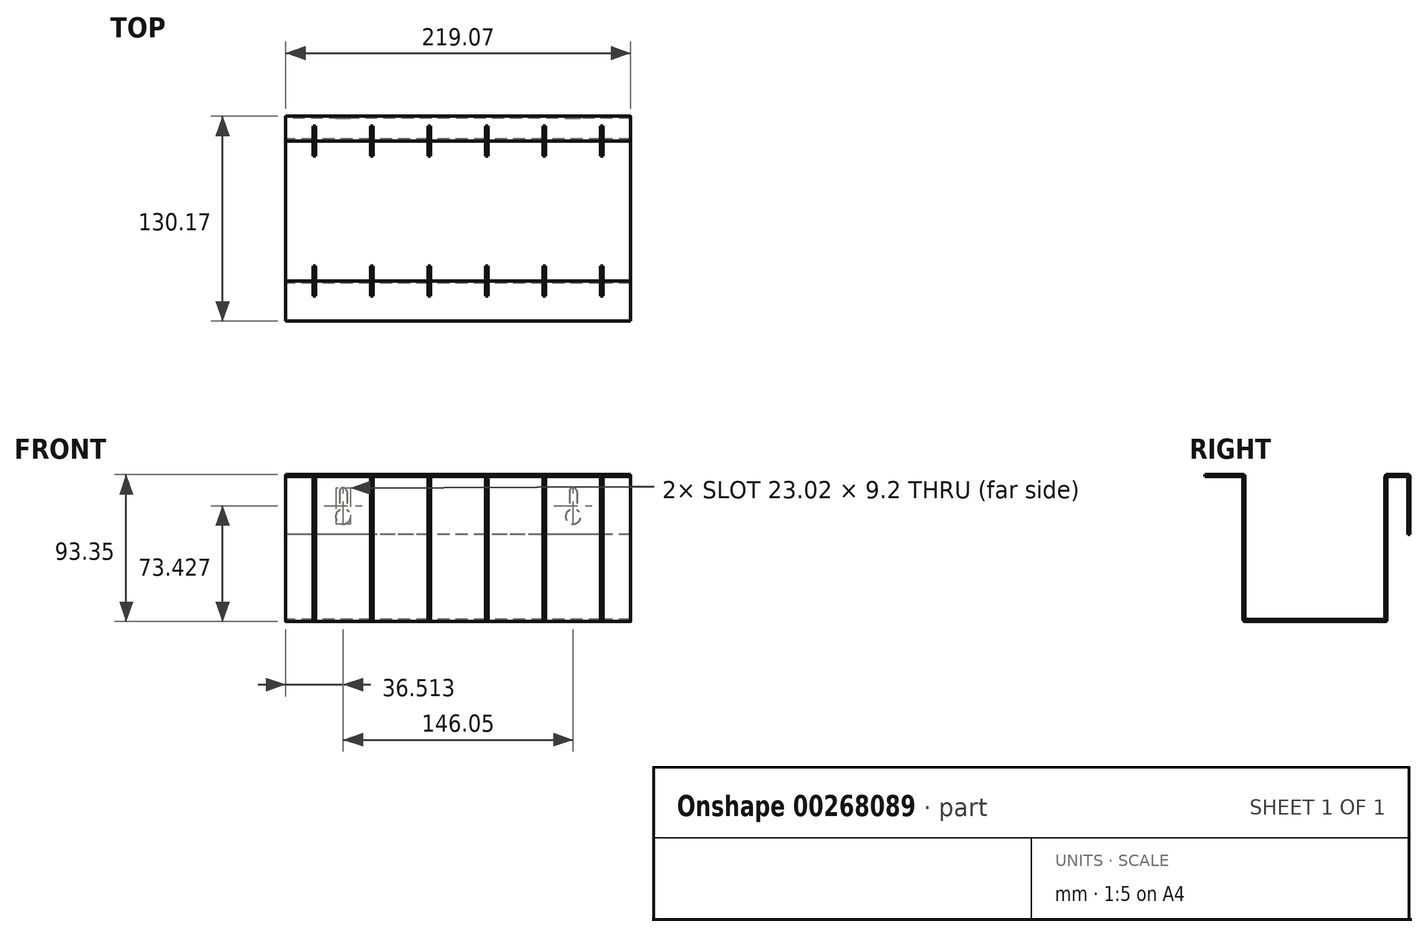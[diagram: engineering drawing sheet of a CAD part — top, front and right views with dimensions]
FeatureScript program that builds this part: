
annotation { "Feature Type Name" : "Feature", "Feature Type Description" : "" }
export const myFeature = defineFeature(function(context is Context, id is Id, definition is map)
    precondition{}
    {
        {
            var Q0;
            Q0=qCreatedBy(makeId("Right.planeOp"),FACE);
            var sketch = newSketch(context, id + "F0", { "sketchPlane" : qUnion([Q0])});
            skLineSegment(sketch, "E0", {"start": v(-62.66, 38.1) * mm, "end": v(-37.26, 38.1) * mm});
            skLineSegment(sketch, "E1", {"start": v(-37.26, 38.1) * mm, "end": v(-37.26, -53.98) * mm});
            skLineSegment(sketch, "E2", {"start": v(-37.26, -53.98) * mm, "end": v(51.64, -53.98) * mm});
            skLineSegment(sketch, "E3", {"start": v(51.64, -53.98) * mm, "end": v(51.64, 38.1) * mm});
            skLineSegment(sketch, "E4", {"start": v(51.64, 38.1) * mm, "end": v(67.51, 38.1) * mm});
            skLineSegment(sketch, "E5", {"start": v(67.51, 38.1) * mm, "end": v(67.51, 0) * mm});
            skLineSegment(sketch, "E6.0", {"start": v(66.24, 36.83) * mm, "end": v(66.24, 0) * mm});
            skLineSegment(sketch, "E6.1", {"start": v(52.9, 36.83) * mm, "end": v(66.24, 36.83) * mm});
            skLineSegment(sketch, "E6.2", {"start": v(-62.66, 36.83) * mm, "end": v(-38.53, 36.83) * mm});
            skLineSegment(sketch, "E6.3", {"start": v(-38.53, 36.83) * mm, "end": v(-38.53, -55.25) * mm});
            skLineSegment(sketch, "E6.4", {"start": v(-38.53, -55.25) * mm, "end": v(52.9, -55.25) * mm});
            skLineSegment(sketch, "E6.5", {"start": v(52.9, -55.25) * mm, "end": v(52.9, 36.83) * mm});
            skLineSegment(sketch, "E7", {"start": v(66.24, 0) * mm, "end": v(67.51, 0) * mm});
            skLineSegment(sketch, "E8", {"start": v(-62.66, 38.1) * mm, "end": v(-62.66, 36.83) * mm});
            skSolve(sketch);
        }
        {
            var Q0;
            Q0 = qSketchRegion(id + "F0", true);
            extrude(context, id + "F1", {"entities" : qUnion([Q0]), "depth" : 219.07 * mm});
        }
        {
            var Q0;
            Q0=makeQuery(id+"F1.opExtrude","SWEPT_FACE",FACE,{"disambiguationData":[OSD([sQuery(id+"F0.wireOp",EDGE,"E0")])]});
            var sketch = newSketch(context, id + "F2", { "sketchPlane" : qUnion([Q0])});
            skLineSegment(sketch, "E9", {"start": v(219.08, -46.79) * mm, "end": v(0, -46.79) * mm, "construction": true});
            skLineSegment(sketch, "E10", {"start": v(17.46, -46.79) * mm, "end": v(17.46, -27.73) * mm});
            skLineSegment(sketch, "E11", {"start": v(19.05, -46.79) * mm, "end": v(19.05, -27.73) * mm});
            skLineSegment(sketch, "E12", {"start": v(19.05, -27.73) * mm, "end": v(17.46, -27.73) * mm});
            skLineSegment(sketch, "E13", {"start": v(17.46, -46.79) * mm, "end": v(19.05, -46.79) * mm});
            skLineSegment(sketch, "E14", {"start": v(201.61, -62.66) * mm, "end": v(201.61, -37.26) * mm, "construction": true});
            skSolve(sketch);
        }
        {
            var Q0;
            Q0 = qSketchRegion(id + "F2", true);
            extrude(context, id + "F3", {"entities" : qUnion([Q0]), "operationType" : NewBodyOperationType.REMOVE, "oppositeDirection" : true, "depth" : 97.28 * mm});
        }
        {
            var Q0;
            Q0=makeQuery(id+"F1.opExtrude","SWEPT_FACE",FACE,{"disambiguationData":[OSD([sQuery(id+"F0.wireOp",EDGE,"E0")])]});
            var sketch = newSketch(context, id + "F4", { "sketchPlane" : qUnion([Q0])});
            skLineSegment(sketch, "E15", {"start": v(53.98, -46.79) * mm, "end": v(53.98, -27.74) * mm});
            skLineSegment(sketch, "E16", {"start": v(55.56, -46.79) * mm, "end": v(55.56, -27.74) * mm});
            skLineSegment(sketch, "E17", {"start": v(55.56, -46.79) * mm, "end": v(53.98, -46.79) * mm});
            skLineSegment(sketch, "E18", {"start": v(55.56, -27.74) * mm, "end": v(53.98, -27.74) * mm});
            skLineSegment(sketch, "E19", {"start": v(90.49, -46.79) * mm, "end": v(90.49, -27.74) * mm});
            skLineSegment(sketch, "E20", {"start": v(92.08, -46.79) * mm, "end": v(92.08, -27.74) * mm});
            skLineSegment(sketch, "E21", {"start": v(92.08, -46.79) * mm, "end": v(90.49, -46.79) * mm});
            skLineSegment(sketch, "E22", {"start": v(92.08, -27.74) * mm, "end": v(90.49, -27.74) * mm});
            skLineSegment(sketch, "E23", {"start": v(127, -46.79) * mm, "end": v(127, -27.74) * mm});
            skLineSegment(sketch, "E24", {"start": v(128.59, -46.79) * mm, "end": v(128.59, -27.74) * mm});
            skLineSegment(sketch, "E25", {"start": v(128.59, -46.79) * mm, "end": v(127, -46.79) * mm});
            skLineSegment(sketch, "E26", {"start": v(128.59, -27.74) * mm, "end": v(127, -27.74) * mm});
            skLineSegment(sketch, "E27", {"start": v(163.51, -46.79) * mm, "end": v(163.51, -27.74) * mm});
            skLineSegment(sketch, "E28", {"start": v(165.1, -46.79) * mm, "end": v(165.1, -27.74) * mm});
            skLineSegment(sketch, "E29", {"start": v(165.1, -46.79) * mm, "end": v(163.51, -46.79) * mm});
            skLineSegment(sketch, "E30", {"start": v(165.1, -27.74) * mm, "end": v(163.51, -27.74) * mm});
            skLineSegment(sketch, "E31", {"start": v(200.03, -46.79) * mm, "end": v(200.03, -27.74) * mm});
            skLineSegment(sketch, "E32", {"start": v(201.61, -46.79) * mm, "end": v(201.61, -27.74) * mm});
            skLineSegment(sketch, "E33", {"start": v(201.61, -46.79) * mm, "end": v(200.03, -46.79) * mm});
            skLineSegment(sketch, "E34", {"start": v(201.61, -27.74) * mm, "end": v(200.03, -27.74) * mm});
            skSolve(sketch);
        }
        {
            var Q0;
            Q0 = qSketchRegion(id + "F4", true);
            extrude(context, id + "F5", {"entities" : qUnion([Q0]), "operationType" : NewBodyOperationType.REMOVE, "endBound" : BoundingType.THROUGH_ALL, "oppositeDirection" : true, "depth" : 108.97 * mm});
        }
        {
            var Q0;
            Q0=makeQuery(id+"F1.opExtrude","SWEPT_FACE",FACE,{"disambiguationData":[OSD([sQuery(id+"F0.wireOp",EDGE,"E0")])]});
            var sketch = newSketch(context, id + "F6", { "sketchPlane" : qUnion([Q0])});
            skSolve(sketch);
        }
        {
            var Q0;
            {var subQ0=sQuery(id+"F0.wireOp",EDGE,"E4");Q0=makeQuery(id+"F7m0HWUFy6dzAhm_1.boolean.opBoolean","MERGE",FACE,{"derivedFrom":[makeQuery(id+"F1.opExtrude","SWEPT_FACE",FACE,{"disambiguationData":[OSD([subQ0])]}),makeQuery(id+"F7m0HWUFy6dzAhm_1.opExtrude","SWEPT_FACE",FACE,{"disambiguationData":[OSD([subQ0])]})]});}
            var sketch = newSketch(context, id + "F7", { "sketchPlane" : qUnion([Q0])});
            skLineSegment(sketch, "E35", {"start": v(17.46, 61.16) * mm, "end": v(17.46, 42.11) * mm});
            skLineSegment(sketch, "E36", {"start": v(19.05, 61.16) * mm, "end": v(19.05, 42.11) * mm});
            skLineSegment(sketch, "E37", {"start": v(17.46, 61.16) * mm, "end": v(19.05, 61.16) * mm});
            skLineSegment(sketch, "E38", {"start": v(17.46, 42.11) * mm, "end": v(19.05, 42.11) * mm});
            skLineSegment(sketch, "E39", {"start": v(53.98, 61.16) * mm, "end": v(53.98, 42.11) * mm});
            skLineSegment(sketch, "E40", {"start": v(55.56, 61.16) * mm, "end": v(55.56, 42.11) * mm});
            skLineSegment(sketch, "E41", {"start": v(55.56, 42.11) * mm, "end": v(53.98, 42.11) * mm});
            skLineSegment(sketch, "E42", {"start": v(55.56, 61.16) * mm, "end": v(53.98, 61.16) * mm});
            skLineSegment(sketch, "E43", {"start": v(90.49, 61.16) * mm, "end": v(90.49, 42.11) * mm});
            skLineSegment(sketch, "E44", {"start": v(90.49, 42.11) * mm, "end": v(92.08, 42.11) * mm});
            skLineSegment(sketch, "E45", {"start": v(92.08, 42.11) * mm, "end": v(92.08, 61.16) * mm});
            skLineSegment(sketch, "E46", {"start": v(90.49, 61.16) * mm, "end": v(92.08, 61.16) * mm});
            skLineSegment(sketch, "E47", {"start": v(127, 61.16) * mm, "end": v(127, 42.11) * mm});
            skLineSegment(sketch, "E48", {"start": v(127, 42.11) * mm, "end": v(128.59, 42.11) * mm});
            skLineSegment(sketch, "E49", {"start": v(128.59, 42.11) * mm, "end": v(128.59, 61.16) * mm});
            skLineSegment(sketch, "E50", {"start": v(127, 61.16) * mm, "end": v(128.59, 61.16) * mm});
            skLineSegment(sketch, "E51", {"start": v(163.51, 61.16) * mm, "end": v(163.51, 42.11) * mm});
            skLineSegment(sketch, "E52", {"start": v(163.51, 42.11) * mm, "end": v(165.1, 42.11) * mm});
            skLineSegment(sketch, "E53", {"start": v(165.1, 42.11) * mm, "end": v(165.1, 61.16) * mm});
            skLineSegment(sketch, "E54", {"start": v(165.1, 61.16) * mm, "end": v(163.51, 61.16) * mm});
            skLineSegment(sketch, "E55", {"start": v(200.03, 61.16) * mm, "end": v(200.03, 42.11) * mm});
            skLineSegment(sketch, "E56", {"start": v(200.03, 42.11) * mm, "end": v(201.61, 42.11) * mm});
            skLineSegment(sketch, "E57", {"start": v(201.61, 42.11) * mm, "end": v(201.61, 61.16) * mm});
            skLineSegment(sketch, "E58", {"start": v(200.03, 61.16) * mm, "end": v(201.61, 61.16) * mm});
            skSolve(sketch);
        }
        {
            var Q0;
            Q0 = qSketchRegion(id + "F7", true);
            extrude(context, id + "F8", {"entities" : qUnion([Q0]), "operationType" : NewBodyOperationType.REMOVE, "oppositeDirection" : true, "depth" : 134.62 * mm});
        }
        {
            var Q0;
            {var subQ0=sQuery(id+"F0.wireOp",EDGE,"E6.1");var subQ1=sQuery(id+"F0.wireOp",EDGE,"E6.0");Q0=makeQuery(id+"F7m0HWUFy6dzAhm_1.boolean.opBoolean","MERGE",EDGE,{"derivedFrom":[makeQuery(id+"F1.opExtrude","SWEPT_EDGE",EDGE,{"disambiguationData":[OSD([subQ1,subQ0])]}),makeQuery(id+"F7m0HWUFy6dzAhm_1.opExtrude","SWEPT_EDGE",EDGE,{"disambiguationData":[OSD([subQ1,subQ0])]})]});}
            var Q1;
            {var subQ0=sQuery(id+"F0.wireOp",EDGE,"E6.5");var subQ1=sQuery(id+"F0.wireOp",EDGE,"E6.1");Q1=makeQuery(id+"F8.boolean.opBoolean","SPLIT",EDGE,{"disambiguationData":[TD([makeQuery(id+"F8.opExtrude","SWEPT_FACE",FACE,{"disambiguationData":[OSD([sQuery(id+"F7.wireOp",EDGE,"E57")])]})])],"derivedFrom":makeQuery(id+"F7m0HWUFy6dzAhm_1.boolean.opBoolean","MERGE",EDGE,{"derivedFrom":[makeQuery(id+"F1.opExtrude","SWEPT_EDGE",EDGE,{"disambiguationData":[OSD([subQ1,subQ0])]}),makeQuery(id+"F7m0HWUFy6dzAhm_1.opExtrude","SWEPT_EDGE",EDGE,{"disambiguationData":[OSD([subQ1,subQ0])]})]})});}
            var Q2;
            {var subQ0=sQuery(id+"F0.wireOp",EDGE,"E6.5");var subQ1=sQuery(id+"F0.wireOp",EDGE,"E6.1");Q2=makeQuery(id+"F8.boolean.opBoolean","SPLIT",EDGE,{"disambiguationData":[TD([makeQuery(id+"F8.opExtrude","SWEPT_FACE",FACE,{"disambiguationData":[OSD([sQuery(id+"F7.wireOp",EDGE,"E53")])]})])],"derivedFrom":makeQuery(id+"F7m0HWUFy6dzAhm_1.boolean.opBoolean","MERGE",EDGE,{"derivedFrom":[makeQuery(id+"F1.opExtrude","SWEPT_EDGE",EDGE,{"disambiguationData":[OSD([subQ1,subQ0])]}),makeQuery(id+"F7m0HWUFy6dzAhm_1.opExtrude","SWEPT_EDGE",EDGE,{"disambiguationData":[OSD([subQ1,subQ0])]})]})});}
            var Q3;
            {var subQ0=sQuery(id+"F0.wireOp",EDGE,"E6.5");var subQ1=sQuery(id+"F0.wireOp",EDGE,"E6.1");Q3=makeQuery(id+"F8.boolean.opBoolean","SPLIT",EDGE,{"disambiguationData":[TD([makeQuery(id+"F8.opExtrude","SWEPT_FACE",FACE,{"disambiguationData":[OSD([sQuery(id+"F7.wireOp",EDGE,"E49")])]})])],"derivedFrom":makeQuery(id+"F7m0HWUFy6dzAhm_1.boolean.opBoolean","MERGE",EDGE,{"derivedFrom":[makeQuery(id+"F1.opExtrude","SWEPT_EDGE",EDGE,{"disambiguationData":[OSD([subQ1,subQ0])]}),makeQuery(id+"F7m0HWUFy6dzAhm_1.opExtrude","SWEPT_EDGE",EDGE,{"disambiguationData":[OSD([subQ1,subQ0])]})]})});}
            var Q4;
            {var subQ0=sQuery(id+"F0.wireOp",EDGE,"E6.5");var subQ1=sQuery(id+"F0.wireOp",EDGE,"E6.1");Q4=makeQuery(id+"F8.boolean.opBoolean","SPLIT",EDGE,{"disambiguationData":[TD([makeQuery(id+"F8.opExtrude","SWEPT_FACE",FACE,{"disambiguationData":[OSD([sQuery(id+"F7.wireOp",EDGE,"E45")])]})])],"derivedFrom":makeQuery(id+"F7m0HWUFy6dzAhm_1.boolean.opBoolean","MERGE",EDGE,{"derivedFrom":[makeQuery(id+"F1.opExtrude","SWEPT_EDGE",EDGE,{"disambiguationData":[OSD([subQ1,subQ0])]}),makeQuery(id+"F7m0HWUFy6dzAhm_1.opExtrude","SWEPT_EDGE",EDGE,{"disambiguationData":[OSD([subQ1,subQ0])]})]})});}
            var Q5;
            {var subQ0=sQuery(id+"F0.wireOp",EDGE,"E6.5");var subQ1=sQuery(id+"F0.wireOp",EDGE,"E6.1");Q5=makeQuery(id+"F8.boolean.opBoolean","SPLIT",EDGE,{"disambiguationData":[TD([makeQuery(id+"F8.opExtrude","SWEPT_FACE",FACE,{"disambiguationData":[OSD([sQuery(id+"F7.wireOp",EDGE,"E40")])]})])],"derivedFrom":makeQuery(id+"F7m0HWUFy6dzAhm_1.boolean.opBoolean","MERGE",EDGE,{"derivedFrom":[makeQuery(id+"F1.opExtrude","SWEPT_EDGE",EDGE,{"disambiguationData":[OSD([subQ1,subQ0])]}),makeQuery(id+"F7m0HWUFy6dzAhm_1.opExtrude","SWEPT_EDGE",EDGE,{"disambiguationData":[OSD([subQ1,subQ0])]})]})});}
            var Q6;
            {var subQ0=sQuery(id+"F0.wireOp",EDGE,"E6.5");var subQ1=sQuery(id+"F0.wireOp",EDGE,"E6.1");Q6=makeQuery(id+"F8.boolean.opBoolean","SPLIT",EDGE,{"disambiguationData":[TD([makeQuery(id+"F8.opExtrude","SWEPT_FACE",FACE,{"disambiguationData":[OSD([sQuery(id+"F7.wireOp",EDGE,"E36")])]})])],"derivedFrom":makeQuery(id+"F7m0HWUFy6dzAhm_1.boolean.opBoolean","MERGE",EDGE,{"derivedFrom":[makeQuery(id+"F1.opExtrude","SWEPT_EDGE",EDGE,{"disambiguationData":[OSD([subQ1,subQ0])]}),makeQuery(id+"F7m0HWUFy6dzAhm_1.opExtrude","SWEPT_EDGE",EDGE,{"disambiguationData":[OSD([subQ1,subQ0])]})]})});}
            var Q7;
            {var subQ0=sQuery(id+"F0.wireOp",EDGE,"E6.5");var subQ1=sQuery(id+"F0.wireOp",EDGE,"E6.1");Q7=makeQuery(id+"F8.boolean.opBoolean","SPLIT",EDGE,{"disambiguationData":[TD([makeQuery(id+"F8.opExtrude","SWEPT_FACE",FACE,{"disambiguationData":[OSD([sQuery(id+"F7.wireOp",EDGE,"E35")])]})])],"derivedFrom":makeQuery(id+"F7m0HWUFy6dzAhm_1.boolean.opBoolean","MERGE",EDGE,{"derivedFrom":[makeQuery(id+"F1.opExtrude","SWEPT_EDGE",EDGE,{"disambiguationData":[OSD([subQ1,subQ0])]}),makeQuery(id+"F7m0HWUFy6dzAhm_1.opExtrude","SWEPT_EDGE",EDGE,{"disambiguationData":[OSD([subQ1,subQ0])]})]})});}
            var Q8;
            {var subQ0=sQuery(id+"F0.wireOp",EDGE,"E6.3");var subQ1=sQuery(id+"F0.wireOp",EDGE,"E6.2");Q8=makeQuery(id+"F7m0HWUFy6dzAhm_1.boolean.opBoolean","MERGE",EDGE,{"derivedFrom":[makeQuery(id+"F5.boolean.opBoolean","SPLIT",EDGE,{"disambiguationData":[TD([makeQuery(id+"F5.opExtrude","SWEPT_FACE",FACE,{"disambiguationData":[OSD([sQuery(id+"F4.wireOp",EDGE,"E32")])]})])],"derivedFrom":makeQuery(id+"F3.boolean.opBoolean","SPLIT",EDGE,{"disambiguationData":[TD([makeQuery(id+"F3.opExtrude","SWEPT_FACE",FACE,{"disambiguationData":[OSD([sQuery(id+"F2.wireOp",EDGE,"E11")])]})])],"derivedFrom":makeQuery(id+"F1.opExtrude","SWEPT_EDGE",EDGE,{"disambiguationData":[OSD([subQ1,subQ0])]})})}),makeQuery(id+"F7m0HWUFy6dzAhm_1.opExtrude","SWEPT_EDGE",EDGE,{"disambiguationData":[OSD([subQ1,subQ0])]})]});}
            var Q9;
            {var subQ0=sQuery(id+"F0.wireOp",EDGE,"E6.2");var subQ2=sQuery(id+"F0.wireOp",EDGE,"E6.3");Q9=makeQuery(id+"F5.boolean.opBoolean","SPLIT",EDGE,{"disambiguationData":[TD([makeQuery(id+"F5.opExtrude","SWEPT_FACE",FACE,{"disambiguationData":[OSD([sQuery(id+"F4.wireOp",EDGE,"E28")])]})])],"derivedFrom":makeQuery(id+"F3.boolean.opBoolean","SPLIT",EDGE,{"disambiguationData":[TD([makeQuery(id+"F3.opExtrude","SWEPT_FACE",FACE,{"disambiguationData":[OSD([sQuery(id+"F2.wireOp",EDGE,"E11")])]})])],"derivedFrom":makeQuery(id+"F1.opExtrude","SWEPT_EDGE",EDGE,{"disambiguationData":[OSD([subQ0,subQ2])]})})});}
            var Q10;
            {var subQ0=sQuery(id+"F0.wireOp",EDGE,"E6.2");var subQ2=sQuery(id+"F0.wireOp",EDGE,"E6.3");Q10=makeQuery(id+"F5.boolean.opBoolean","SPLIT",EDGE,{"disambiguationData":[TD([makeQuery(id+"F5.opExtrude","SWEPT_FACE",FACE,{"disambiguationData":[OSD([sQuery(id+"F4.wireOp",EDGE,"E24")])]})])],"derivedFrom":makeQuery(id+"F3.boolean.opBoolean","SPLIT",EDGE,{"disambiguationData":[TD([makeQuery(id+"F3.opExtrude","SWEPT_FACE",FACE,{"disambiguationData":[OSD([sQuery(id+"F2.wireOp",EDGE,"E11")])]})])],"derivedFrom":makeQuery(id+"F1.opExtrude","SWEPT_EDGE",EDGE,{"disambiguationData":[OSD([subQ0,subQ2])]})})});}
            var Q11;
            {var subQ0=sQuery(id+"F0.wireOp",EDGE,"E6.2");var subQ2=sQuery(id+"F0.wireOp",EDGE,"E6.3");Q11=makeQuery(id+"F5.boolean.opBoolean","SPLIT",EDGE,{"disambiguationData":[TD([makeQuery(id+"F5.opExtrude","SWEPT_FACE",FACE,{"disambiguationData":[OSD([sQuery(id+"F4.wireOp",EDGE,"E20")])]})])],"derivedFrom":makeQuery(id+"F3.boolean.opBoolean","SPLIT",EDGE,{"disambiguationData":[TD([makeQuery(id+"F3.opExtrude","SWEPT_FACE",FACE,{"disambiguationData":[OSD([sQuery(id+"F2.wireOp",EDGE,"E11")])]})])],"derivedFrom":makeQuery(id+"F1.opExtrude","SWEPT_EDGE",EDGE,{"disambiguationData":[OSD([subQ0,subQ2])]})})});}
            var Q12;
            {var subQ0=sQuery(id+"F0.wireOp",EDGE,"E6.2");var subQ2=sQuery(id+"F0.wireOp",EDGE,"E6.3");Q12=makeQuery(id+"F5.boolean.opBoolean","SPLIT",EDGE,{"disambiguationData":[TD([makeQuery(id+"F5.opExtrude","SWEPT_FACE",FACE,{"disambiguationData":[OSD([sQuery(id+"F4.wireOp",EDGE,"E16")])]})])],"derivedFrom":makeQuery(id+"F3.boolean.opBoolean","SPLIT",EDGE,{"disambiguationData":[TD([makeQuery(id+"F3.opExtrude","SWEPT_FACE",FACE,{"disambiguationData":[OSD([sQuery(id+"F2.wireOp",EDGE,"E11")])]})])],"derivedFrom":makeQuery(id+"F1.opExtrude","SWEPT_EDGE",EDGE,{"disambiguationData":[OSD([subQ0,subQ2])]})})});}
            var Q13;
            {var subQ0=sQuery(id+"F0.wireOp",EDGE,"E6.2");var subQ2=sQuery(id+"F0.wireOp",EDGE,"E6.3");var subQ4=makeQuery(id+"F3.opExtrude","SWEPT_FACE",FACE,{"disambiguationData":[OSD([sQuery(id+"F2.wireOp",EDGE,"E11")])]});Q13=makeQuery(id+"F5.boolean.opBoolean","SPLIT",EDGE,{"disambiguationData":[TD([makeQuery(id+"F3.boolean.opBoolean","COPY",FACE,{"derivedFrom":subQ4})])],"derivedFrom":makeQuery(id+"F3.boolean.opBoolean","SPLIT",EDGE,{"disambiguationData":[TD([subQ4])],"derivedFrom":makeQuery(id+"F1.opExtrude","SWEPT_EDGE",EDGE,{"disambiguationData":[OSD([subQ0,subQ2])]})})});}
            var Q14;
            {var subQ0=sQuery(id+"F0.wireOp",EDGE,"E6.3");var subQ1=sQuery(id+"F0.wireOp",EDGE,"E6.2");Q14=makeQuery(id+"F3.boolean.opBoolean","SPLIT",EDGE,{"disambiguationData":[TD([makeQuery(id+"F3.opExtrude","SWEPT_FACE",FACE,{"disambiguationData":[OSD([sQuery(id+"F2.wireOp",EDGE,"E10")])]})])],"derivedFrom":makeQuery(id+"F1.opExtrude","SWEPT_EDGE",EDGE,{"disambiguationData":[OSD([subQ1,subQ0])]})});}
            var Q15;
            {var subQ0=sQuery(id+"F0.wireOp",EDGE,"E3");var subQ1=sQuery(id+"F0.wireOp",EDGE,"E2");Q15=makeQuery(id+"F8.boolean.opBoolean","SPLIT",EDGE,{"disambiguationData":[TD([makeQuery(id+"F8.opExtrude","SWEPT_FACE",FACE,{"disambiguationData":[OSD([sQuery(id+"F7.wireOp",EDGE,"E57")])]})])],"derivedFrom":makeQuery(id+"F7m0HWUFy6dzAhm_1.boolean.opBoolean","MERGE",EDGE,{"derivedFrom":[makeQuery(id+"F1.opExtrude","SWEPT_EDGE",EDGE,{"disambiguationData":[OSD([subQ1,subQ0])]}),makeQuery(id+"F7m0HWUFy6dzAhm_1.opExtrude","SWEPT_EDGE",EDGE,{"disambiguationData":[OSD([subQ1,subQ0])]})]})});}
            var Q16;
            {var subQ0=sQuery(id+"F0.wireOp",EDGE,"E3");var subQ1=sQuery(id+"F0.wireOp",EDGE,"E2");Q16=makeQuery(id+"F8.boolean.opBoolean","SPLIT",EDGE,{"disambiguationData":[TD([makeQuery(id+"F8.opExtrude","SWEPT_FACE",FACE,{"disambiguationData":[OSD([sQuery(id+"F7.wireOp",EDGE,"E53")])]})])],"derivedFrom":makeQuery(id+"F7m0HWUFy6dzAhm_1.boolean.opBoolean","MERGE",EDGE,{"derivedFrom":[makeQuery(id+"F1.opExtrude","SWEPT_EDGE",EDGE,{"disambiguationData":[OSD([subQ1,subQ0])]}),makeQuery(id+"F7m0HWUFy6dzAhm_1.opExtrude","SWEPT_EDGE",EDGE,{"disambiguationData":[OSD([subQ1,subQ0])]})]})});}
            var Q17;
            {var subQ0=sQuery(id+"F0.wireOp",EDGE,"E3");var subQ1=sQuery(id+"F0.wireOp",EDGE,"E2");Q17=makeQuery(id+"F8.boolean.opBoolean","SPLIT",EDGE,{"disambiguationData":[TD([makeQuery(id+"F8.opExtrude","SWEPT_FACE",FACE,{"disambiguationData":[OSD([sQuery(id+"F7.wireOp",EDGE,"E49")])]})])],"derivedFrom":makeQuery(id+"F7m0HWUFy6dzAhm_1.boolean.opBoolean","MERGE",EDGE,{"derivedFrom":[makeQuery(id+"F1.opExtrude","SWEPT_EDGE",EDGE,{"disambiguationData":[OSD([subQ1,subQ0])]}),makeQuery(id+"F7m0HWUFy6dzAhm_1.opExtrude","SWEPT_EDGE",EDGE,{"disambiguationData":[OSD([subQ1,subQ0])]})]})});}
            var Q18;
            {var subQ0=sQuery(id+"F0.wireOp",EDGE,"E3");var subQ1=sQuery(id+"F0.wireOp",EDGE,"E2");Q18=makeQuery(id+"F8.boolean.opBoolean","SPLIT",EDGE,{"disambiguationData":[TD([makeQuery(id+"F8.opExtrude","SWEPT_FACE",FACE,{"disambiguationData":[OSD([sQuery(id+"F7.wireOp",EDGE,"E45")])]})])],"derivedFrom":makeQuery(id+"F7m0HWUFy6dzAhm_1.boolean.opBoolean","MERGE",EDGE,{"derivedFrom":[makeQuery(id+"F1.opExtrude","SWEPT_EDGE",EDGE,{"disambiguationData":[OSD([subQ1,subQ0])]}),makeQuery(id+"F7m0HWUFy6dzAhm_1.opExtrude","SWEPT_EDGE",EDGE,{"disambiguationData":[OSD([subQ1,subQ0])]})]})});}
            var Q19;
            {var subQ0=sQuery(id+"F0.wireOp",EDGE,"E3");var subQ1=sQuery(id+"F0.wireOp",EDGE,"E2");Q19=makeQuery(id+"F8.boolean.opBoolean","SPLIT",EDGE,{"disambiguationData":[TD([makeQuery(id+"F8.opExtrude","SWEPT_FACE",FACE,{"disambiguationData":[OSD([sQuery(id+"F7.wireOp",EDGE,"E40")])]})])],"derivedFrom":makeQuery(id+"F7m0HWUFy6dzAhm_1.boolean.opBoolean","MERGE",EDGE,{"derivedFrom":[makeQuery(id+"F1.opExtrude","SWEPT_EDGE",EDGE,{"disambiguationData":[OSD([subQ1,subQ0])]}),makeQuery(id+"F7m0HWUFy6dzAhm_1.opExtrude","SWEPT_EDGE",EDGE,{"disambiguationData":[OSD([subQ1,subQ0])]})]})});}
            var Q20;
            {var subQ0=sQuery(id+"F0.wireOp",EDGE,"E3");var subQ1=sQuery(id+"F0.wireOp",EDGE,"E2");Q20=makeQuery(id+"F8.boolean.opBoolean","SPLIT",EDGE,{"disambiguationData":[TD([makeQuery(id+"F8.opExtrude","SWEPT_FACE",FACE,{"disambiguationData":[OSD([sQuery(id+"F7.wireOp",EDGE,"E36")])]})])],"derivedFrom":makeQuery(id+"F7m0HWUFy6dzAhm_1.boolean.opBoolean","MERGE",EDGE,{"derivedFrom":[makeQuery(id+"F1.opExtrude","SWEPT_EDGE",EDGE,{"disambiguationData":[OSD([subQ1,subQ0])]}),makeQuery(id+"F7m0HWUFy6dzAhm_1.opExtrude","SWEPT_EDGE",EDGE,{"disambiguationData":[OSD([subQ1,subQ0])]})]})});}
            var Q21;
            {var subQ0=sQuery(id+"F0.wireOp",EDGE,"E2");var subQ1=sQuery(id+"F0.wireOp",EDGE,"E3");Q21=makeQuery(id+"F8.boolean.opBoolean","SPLIT",EDGE,{"disambiguationData":[TD([makeQuery(id+"F8.opExtrude","SWEPT_FACE",FACE,{"disambiguationData":[OSD([sQuery(id+"F7.wireOp",EDGE,"E35")])]})])],"derivedFrom":makeQuery(id+"F7m0HWUFy6dzAhm_1.boolean.opBoolean","MERGE",EDGE,{"derivedFrom":[makeQuery(id+"F1.opExtrude","SWEPT_EDGE",EDGE,{"disambiguationData":[OSD([subQ0,subQ1])]}),makeQuery(id+"F7m0HWUFy6dzAhm_1.opExtrude","SWEPT_EDGE",EDGE,{"disambiguationData":[OSD([subQ0,subQ1])]})]})});}
            var Q22;
            {var subQ0=sQuery(id+"F0.wireOp",EDGE,"E2");var subQ1=sQuery(id+"F0.wireOp",EDGE,"E1");Q22=makeQuery(id+"F7m0HWUFy6dzAhm_1.boolean.opBoolean","MERGE",EDGE,{"derivedFrom":[makeQuery(id+"F5.boolean.opBoolean","SPLIT",EDGE,{"disambiguationData":[TD([makeQuery(id+"F5.opExtrude","SWEPT_FACE",FACE,{"disambiguationData":[OSD([sQuery(id+"F4.wireOp",EDGE,"E32")])]})])],"derivedFrom":makeQuery(id+"F3.boolean.opBoolean","SPLIT",EDGE,{"disambiguationData":[TD([makeQuery(id+"F3.opExtrude","SWEPT_FACE",FACE,{"disambiguationData":[OSD([sQuery(id+"F2.wireOp",EDGE,"E11")])]})])],"derivedFrom":makeQuery(id+"F1.opExtrude","SWEPT_EDGE",EDGE,{"disambiguationData":[OSD([subQ1,subQ0])]})})}),makeQuery(id+"F7m0HWUFy6dzAhm_1.opExtrude","SWEPT_EDGE",EDGE,{"disambiguationData":[OSD([subQ1,subQ0])]})]});}
            var Q23;
            {var subQ0=sQuery(id+"F0.wireOp",EDGE,"E1");var subQ2=sQuery(id+"F0.wireOp",EDGE,"E2");Q23=makeQuery(id+"F5.boolean.opBoolean","SPLIT",EDGE,{"disambiguationData":[TD([makeQuery(id+"F5.opExtrude","SWEPT_FACE",FACE,{"disambiguationData":[OSD([sQuery(id+"F4.wireOp",EDGE,"E28")])]})])],"derivedFrom":makeQuery(id+"F3.boolean.opBoolean","SPLIT",EDGE,{"disambiguationData":[TD([makeQuery(id+"F3.opExtrude","SWEPT_FACE",FACE,{"disambiguationData":[OSD([sQuery(id+"F2.wireOp",EDGE,"E11")])]})])],"derivedFrom":makeQuery(id+"F1.opExtrude","SWEPT_EDGE",EDGE,{"disambiguationData":[OSD([subQ0,subQ2])]})})});}
            var Q24;
            {var subQ0=sQuery(id+"F0.wireOp",EDGE,"E1");var subQ2=sQuery(id+"F0.wireOp",EDGE,"E2");Q24=makeQuery(id+"F5.boolean.opBoolean","SPLIT",EDGE,{"disambiguationData":[TD([makeQuery(id+"F5.opExtrude","SWEPT_FACE",FACE,{"disambiguationData":[OSD([sQuery(id+"F4.wireOp",EDGE,"E24")])]})])],"derivedFrom":makeQuery(id+"F3.boolean.opBoolean","SPLIT",EDGE,{"disambiguationData":[TD([makeQuery(id+"F3.opExtrude","SWEPT_FACE",FACE,{"disambiguationData":[OSD([sQuery(id+"F2.wireOp",EDGE,"E11")])]})])],"derivedFrom":makeQuery(id+"F1.opExtrude","SWEPT_EDGE",EDGE,{"disambiguationData":[OSD([subQ0,subQ2])]})})});}
            var Q25;
            {var subQ0=sQuery(id+"F0.wireOp",EDGE,"E1");var subQ2=sQuery(id+"F0.wireOp",EDGE,"E2");Q25=makeQuery(id+"F5.boolean.opBoolean","SPLIT",EDGE,{"disambiguationData":[TD([makeQuery(id+"F5.opExtrude","SWEPT_FACE",FACE,{"disambiguationData":[OSD([sQuery(id+"F4.wireOp",EDGE,"E20")])]})])],"derivedFrom":makeQuery(id+"F3.boolean.opBoolean","SPLIT",EDGE,{"disambiguationData":[TD([makeQuery(id+"F3.opExtrude","SWEPT_FACE",FACE,{"disambiguationData":[OSD([sQuery(id+"F2.wireOp",EDGE,"E11")])]})])],"derivedFrom":makeQuery(id+"F1.opExtrude","SWEPT_EDGE",EDGE,{"disambiguationData":[OSD([subQ0,subQ2])]})})});}
            var Q26;
            {var subQ0=sQuery(id+"F0.wireOp",EDGE,"E1");var subQ2=sQuery(id+"F0.wireOp",EDGE,"E2");Q26=makeQuery(id+"F5.boolean.opBoolean","SPLIT",EDGE,{"disambiguationData":[TD([makeQuery(id+"F5.opExtrude","SWEPT_FACE",FACE,{"disambiguationData":[OSD([sQuery(id+"F4.wireOp",EDGE,"E16")])]})])],"derivedFrom":makeQuery(id+"F3.boolean.opBoolean","SPLIT",EDGE,{"disambiguationData":[TD([makeQuery(id+"F3.opExtrude","SWEPT_FACE",FACE,{"disambiguationData":[OSD([sQuery(id+"F2.wireOp",EDGE,"E11")])]})])],"derivedFrom":makeQuery(id+"F1.opExtrude","SWEPT_EDGE",EDGE,{"disambiguationData":[OSD([subQ0,subQ2])]})})});}
            var Q27;
            {var subQ0=sQuery(id+"F0.wireOp",EDGE,"E1");var subQ2=sQuery(id+"F0.wireOp",EDGE,"E2");var subQ4=makeQuery(id+"F3.opExtrude","SWEPT_FACE",FACE,{"disambiguationData":[OSD([sQuery(id+"F2.wireOp",EDGE,"E11")])]});Q27=makeQuery(id+"F5.boolean.opBoolean","SPLIT",EDGE,{"disambiguationData":[TD([makeQuery(id+"F3.boolean.opBoolean","COPY",FACE,{"derivedFrom":subQ4})])],"derivedFrom":makeQuery(id+"F3.boolean.opBoolean","SPLIT",EDGE,{"disambiguationData":[TD([subQ4])],"derivedFrom":makeQuery(id+"F1.opExtrude","SWEPT_EDGE",EDGE,{"disambiguationData":[OSD([subQ0,subQ2])]})})});}
            var Q28;
            {var subQ0=sQuery(id+"F0.wireOp",EDGE,"E2");var subQ1=sQuery(id+"F0.wireOp",EDGE,"E1");Q28=makeQuery(id+"F3.boolean.opBoolean","SPLIT",EDGE,{"disambiguationData":[TD([makeQuery(id+"F3.opExtrude","SWEPT_FACE",FACE,{"disambiguationData":[OSD([sQuery(id+"F2.wireOp",EDGE,"E10")])]})])],"derivedFrom":makeQuery(id+"F1.opExtrude","SWEPT_EDGE",EDGE,{"disambiguationData":[OSD([subQ1,subQ0])]})});}
            fillet(context, id + "F9", {"entities" : qUnion([Q0, Q1, Q2, Q3, Q4, Q5, Q6, Q7, Q8, Q9, Q10, Q11, Q12, Q13, Q14, Q15, Q16, Q17, Q18, Q19, Q20, Q21, Q22, Q23, Q24, Q25, Q26, Q27, Q28]), "radius" : 0.5 * mm, "tangentPropagation" : true, "allowEdgeOverflow" : false});
        }
        {
            var Q0;
            {var subQ0=sQuery(id+"F0.wireOp",EDGE,"E5");var subQ1=sQuery(id+"F0.wireOp",EDGE,"E4");Q0=makeQuery(id+"F7m0HWUFy6dzAhm_1.boolean.opBoolean","MERGE",EDGE,{"derivedFrom":[makeQuery(id+"F1.opExtrude","SWEPT_EDGE",EDGE,{"disambiguationData":[OSD([subQ1,subQ0])]}),makeQuery(id+"F7m0HWUFy6dzAhm_1.opExtrude","SWEPT_EDGE",EDGE,{"disambiguationData":[OSD([subQ1,subQ0])]})]});}
            var Q1;
            {var subQ0=sQuery(id+"F0.wireOp",EDGE,"E3");var subQ1=sQuery(id+"F0.wireOp",EDGE,"E4");Q1=makeQuery(id+"F8.boolean.opBoolean","SPLIT",EDGE,{"disambiguationData":[TD([makeQuery(id+"F8.opExtrude","SWEPT_FACE",FACE,{"disambiguationData":[OSD([sQuery(id+"F7.wireOp",EDGE,"E35")])]})])],"derivedFrom":makeQuery(id+"F7m0HWUFy6dzAhm_1.boolean.opBoolean","MERGE",EDGE,{"derivedFrom":[makeQuery(id+"F1.opExtrude","SWEPT_EDGE",EDGE,{"disambiguationData":[OSD([subQ0,subQ1])]}),makeQuery(id+"F7m0HWUFy6dzAhm_1.opExtrude","SWEPT_EDGE",EDGE,{"disambiguationData":[OSD([subQ0,subQ1])]})]})});}
            var Q2;
            {var subQ0=sQuery(id+"F0.wireOp",EDGE,"E3");var subQ1=sQuery(id+"F0.wireOp",EDGE,"E4");Q2=makeQuery(id+"F8.boolean.opBoolean","SPLIT",EDGE,{"disambiguationData":[TD([makeQuery(id+"F8.opExtrude","SWEPT_FACE",FACE,{"disambiguationData":[OSD([sQuery(id+"F7.wireOp",EDGE,"E36")])]})])],"derivedFrom":makeQuery(id+"F7m0HWUFy6dzAhm_1.boolean.opBoolean","MERGE",EDGE,{"derivedFrom":[makeQuery(id+"F1.opExtrude","SWEPT_EDGE",EDGE,{"disambiguationData":[OSD([subQ0,subQ1])]}),makeQuery(id+"F7m0HWUFy6dzAhm_1.opExtrude","SWEPT_EDGE",EDGE,{"disambiguationData":[OSD([subQ0,subQ1])]})]})});}
            var Q3;
            {var subQ0=sQuery(id+"F0.wireOp",EDGE,"E3");var subQ1=sQuery(id+"F0.wireOp",EDGE,"E4");Q3=makeQuery(id+"F8.boolean.opBoolean","SPLIT",EDGE,{"disambiguationData":[TD([makeQuery(id+"F8.opExtrude","SWEPT_FACE",FACE,{"disambiguationData":[OSD([sQuery(id+"F7.wireOp",EDGE,"E40")])]})])],"derivedFrom":makeQuery(id+"F7m0HWUFy6dzAhm_1.boolean.opBoolean","MERGE",EDGE,{"derivedFrom":[makeQuery(id+"F1.opExtrude","SWEPT_EDGE",EDGE,{"disambiguationData":[OSD([subQ0,subQ1])]}),makeQuery(id+"F7m0HWUFy6dzAhm_1.opExtrude","SWEPT_EDGE",EDGE,{"disambiguationData":[OSD([subQ0,subQ1])]})]})});}
            var Q4;
            {var subQ0=sQuery(id+"F0.wireOp",EDGE,"E3");var subQ1=sQuery(id+"F0.wireOp",EDGE,"E4");Q4=makeQuery(id+"F8.boolean.opBoolean","SPLIT",EDGE,{"disambiguationData":[TD([makeQuery(id+"F8.opExtrude","SWEPT_FACE",FACE,{"disambiguationData":[OSD([sQuery(id+"F7.wireOp",EDGE,"E45")])]})])],"derivedFrom":makeQuery(id+"F7m0HWUFy6dzAhm_1.boolean.opBoolean","MERGE",EDGE,{"derivedFrom":[makeQuery(id+"F1.opExtrude","SWEPT_EDGE",EDGE,{"disambiguationData":[OSD([subQ0,subQ1])]}),makeQuery(id+"F7m0HWUFy6dzAhm_1.opExtrude","SWEPT_EDGE",EDGE,{"disambiguationData":[OSD([subQ0,subQ1])]})]})});}
            var Q5;
            {var subQ0=sQuery(id+"F0.wireOp",EDGE,"E3");var subQ1=sQuery(id+"F0.wireOp",EDGE,"E4");Q5=makeQuery(id+"F8.boolean.opBoolean","SPLIT",EDGE,{"disambiguationData":[TD([makeQuery(id+"F8.opExtrude","SWEPT_FACE",FACE,{"disambiguationData":[OSD([sQuery(id+"F7.wireOp",EDGE,"E49")])]})])],"derivedFrom":makeQuery(id+"F7m0HWUFy6dzAhm_1.boolean.opBoolean","MERGE",EDGE,{"derivedFrom":[makeQuery(id+"F1.opExtrude","SWEPT_EDGE",EDGE,{"disambiguationData":[OSD([subQ0,subQ1])]}),makeQuery(id+"F7m0HWUFy6dzAhm_1.opExtrude","SWEPT_EDGE",EDGE,{"disambiguationData":[OSD([subQ0,subQ1])]})]})});}
            var Q6;
            {var subQ0=sQuery(id+"F0.wireOp",EDGE,"E3");var subQ1=sQuery(id+"F0.wireOp",EDGE,"E4");Q6=makeQuery(id+"F8.boolean.opBoolean","SPLIT",EDGE,{"disambiguationData":[TD([makeQuery(id+"F8.opExtrude","SWEPT_FACE",FACE,{"disambiguationData":[OSD([sQuery(id+"F7.wireOp",EDGE,"E53")])]})])],"derivedFrom":makeQuery(id+"F7m0HWUFy6dzAhm_1.boolean.opBoolean","MERGE",EDGE,{"derivedFrom":[makeQuery(id+"F1.opExtrude","SWEPT_EDGE",EDGE,{"disambiguationData":[OSD([subQ0,subQ1])]}),makeQuery(id+"F7m0HWUFy6dzAhm_1.opExtrude","SWEPT_EDGE",EDGE,{"disambiguationData":[OSD([subQ0,subQ1])]})]})});}
            var Q7;
            {var subQ0=sQuery(id+"F0.wireOp",EDGE,"E3");var subQ1=sQuery(id+"F0.wireOp",EDGE,"E4");Q7=makeQuery(id+"F8.boolean.opBoolean","SPLIT",EDGE,{"disambiguationData":[TD([makeQuery(id+"F8.opExtrude","SWEPT_FACE",FACE,{"disambiguationData":[OSD([sQuery(id+"F7.wireOp",EDGE,"E57")])]})])],"derivedFrom":makeQuery(id+"F7m0HWUFy6dzAhm_1.boolean.opBoolean","MERGE",EDGE,{"derivedFrom":[makeQuery(id+"F1.opExtrude","SWEPT_EDGE",EDGE,{"disambiguationData":[OSD([subQ0,subQ1])]}),makeQuery(id+"F7m0HWUFy6dzAhm_1.opExtrude","SWEPT_EDGE",EDGE,{"disambiguationData":[OSD([subQ0,subQ1])]})]})});}
            var Q8;
            {var subQ0=sQuery(id+"F0.wireOp",EDGE,"E1");var subQ1=sQuery(id+"F0.wireOp",EDGE,"E0");Q8=makeQuery(id+"F7m0HWUFy6dzAhm_1.boolean.opBoolean","MERGE",EDGE,{"derivedFrom":[makeQuery(id+"F5.boolean.opBoolean","SPLIT",EDGE,{"disambiguationData":[TD([makeQuery(id+"F5.opExtrude","SWEPT_FACE",FACE,{"disambiguationData":[OSD([sQuery(id+"F4.wireOp",EDGE,"E32")])]})])],"derivedFrom":makeQuery(id+"F3.boolean.opBoolean","SPLIT",EDGE,{"disambiguationData":[TD([makeQuery(id+"F3.opExtrude","SWEPT_FACE",FACE,{"disambiguationData":[OSD([sQuery(id+"F2.wireOp",EDGE,"E11")])]})])],"derivedFrom":makeQuery(id+"F1.opExtrude","SWEPT_EDGE",EDGE,{"disambiguationData":[OSD([subQ1,subQ0])]})})}),makeQuery(id+"F7m0HWUFy6dzAhm_1.opExtrude","SWEPT_EDGE",EDGE,{"disambiguationData":[OSD([subQ1,subQ0])]})]});}
            var Q9;
            {var subQ0=sQuery(id+"F0.wireOp",EDGE,"E0");var subQ2=sQuery(id+"F0.wireOp",EDGE,"E1");Q9=makeQuery(id+"F5.boolean.opBoolean","SPLIT",EDGE,{"disambiguationData":[TD([makeQuery(id+"F5.opExtrude","SWEPT_FACE",FACE,{"disambiguationData":[OSD([sQuery(id+"F4.wireOp",EDGE,"E28")])]})])],"derivedFrom":makeQuery(id+"F3.boolean.opBoolean","SPLIT",EDGE,{"disambiguationData":[TD([makeQuery(id+"F3.opExtrude","SWEPT_FACE",FACE,{"disambiguationData":[OSD([sQuery(id+"F2.wireOp",EDGE,"E11")])]})])],"derivedFrom":makeQuery(id+"F1.opExtrude","SWEPT_EDGE",EDGE,{"disambiguationData":[OSD([subQ0,subQ2])]})})});}
            var Q10;
            {var subQ0=sQuery(id+"F0.wireOp",EDGE,"E0");var subQ2=sQuery(id+"F0.wireOp",EDGE,"E1");Q10=makeQuery(id+"F5.boolean.opBoolean","SPLIT",EDGE,{"disambiguationData":[TD([makeQuery(id+"F5.opExtrude","SWEPT_FACE",FACE,{"disambiguationData":[OSD([sQuery(id+"F4.wireOp",EDGE,"E24")])]})])],"derivedFrom":makeQuery(id+"F3.boolean.opBoolean","SPLIT",EDGE,{"disambiguationData":[TD([makeQuery(id+"F3.opExtrude","SWEPT_FACE",FACE,{"disambiguationData":[OSD([sQuery(id+"F2.wireOp",EDGE,"E11")])]})])],"derivedFrom":makeQuery(id+"F1.opExtrude","SWEPT_EDGE",EDGE,{"disambiguationData":[OSD([subQ0,subQ2])]})})});}
            var Q11;
            {var subQ0=sQuery(id+"F0.wireOp",EDGE,"E0");var subQ2=sQuery(id+"F0.wireOp",EDGE,"E1");Q11=makeQuery(id+"F5.boolean.opBoolean","SPLIT",EDGE,{"disambiguationData":[TD([makeQuery(id+"F5.opExtrude","SWEPT_FACE",FACE,{"disambiguationData":[OSD([sQuery(id+"F4.wireOp",EDGE,"E20")])]})])],"derivedFrom":makeQuery(id+"F3.boolean.opBoolean","SPLIT",EDGE,{"disambiguationData":[TD([makeQuery(id+"F3.opExtrude","SWEPT_FACE",FACE,{"disambiguationData":[OSD([sQuery(id+"F2.wireOp",EDGE,"E11")])]})])],"derivedFrom":makeQuery(id+"F1.opExtrude","SWEPT_EDGE",EDGE,{"disambiguationData":[OSD([subQ0,subQ2])]})})});}
            var Q12;
            {var subQ0=sQuery(id+"F0.wireOp",EDGE,"E0");var subQ2=sQuery(id+"F0.wireOp",EDGE,"E1");Q12=makeQuery(id+"F5.boolean.opBoolean","SPLIT",EDGE,{"disambiguationData":[TD([makeQuery(id+"F5.opExtrude","SWEPT_FACE",FACE,{"disambiguationData":[OSD([sQuery(id+"F4.wireOp",EDGE,"E16")])]})])],"derivedFrom":makeQuery(id+"F3.boolean.opBoolean","SPLIT",EDGE,{"disambiguationData":[TD([makeQuery(id+"F3.opExtrude","SWEPT_FACE",FACE,{"disambiguationData":[OSD([sQuery(id+"F2.wireOp",EDGE,"E11")])]})])],"derivedFrom":makeQuery(id+"F1.opExtrude","SWEPT_EDGE",EDGE,{"disambiguationData":[OSD([subQ0,subQ2])]})})});}
            var Q13;
            {var subQ0=sQuery(id+"F0.wireOp",EDGE,"E0");var subQ2=sQuery(id+"F0.wireOp",EDGE,"E1");var subQ4=makeQuery(id+"F3.opExtrude","SWEPT_FACE",FACE,{"disambiguationData":[OSD([sQuery(id+"F2.wireOp",EDGE,"E11")])]});Q13=makeQuery(id+"F5.boolean.opBoolean","SPLIT",EDGE,{"disambiguationData":[TD([makeQuery(id+"F3.boolean.opBoolean","COPY",FACE,{"derivedFrom":subQ4})])],"derivedFrom":makeQuery(id+"F3.boolean.opBoolean","SPLIT",EDGE,{"disambiguationData":[TD([subQ4])],"derivedFrom":makeQuery(id+"F1.opExtrude","SWEPT_EDGE",EDGE,{"disambiguationData":[OSD([subQ0,subQ2])]})})});}
            var Q14;
            {var subQ0=sQuery(id+"F0.wireOp",EDGE,"E0");var subQ1=sQuery(id+"F0.wireOp",EDGE,"E1");Q14=makeQuery(id+"F3.boolean.opBoolean","SPLIT",EDGE,{"disambiguationData":[TD([makeQuery(id+"F3.opExtrude","SWEPT_FACE",FACE,{"disambiguationData":[OSD([sQuery(id+"F2.wireOp",EDGE,"E10")])]})])],"derivedFrom":makeQuery(id+"F1.opExtrude","SWEPT_EDGE",EDGE,{"disambiguationData":[OSD([subQ0,subQ1])]})});}
            var Q15;
            {var subQ0=sQuery(id+"F0.wireOp",EDGE,"E6.5");var subQ1=sQuery(id+"F0.wireOp",EDGE,"E6.4");Q15=makeQuery(id+"F8.boolean.opBoolean","SPLIT",EDGE,{"disambiguationData":[TD([makeQuery(id+"F8.opExtrude","SWEPT_FACE",FACE,{"disambiguationData":[OSD([sQuery(id+"F7.wireOp",EDGE,"E57")])]})])],"derivedFrom":makeQuery(id+"F7m0HWUFy6dzAhm_1.boolean.opBoolean","MERGE",EDGE,{"derivedFrom":[makeQuery(id+"F1.opExtrude","SWEPT_EDGE",EDGE,{"disambiguationData":[OSD([subQ1,subQ0])]}),makeQuery(id+"F7m0HWUFy6dzAhm_1.opExtrude","SWEPT_EDGE",EDGE,{"disambiguationData":[OSD([subQ1,subQ0])]})]})});}
            var Q16;
            {var subQ0=sQuery(id+"F0.wireOp",EDGE,"E6.5");var subQ1=sQuery(id+"F0.wireOp",EDGE,"E6.4");Q16=makeQuery(id+"F8.boolean.opBoolean","SPLIT",EDGE,{"disambiguationData":[TD([makeQuery(id+"F8.opExtrude","SWEPT_FACE",FACE,{"disambiguationData":[OSD([sQuery(id+"F7.wireOp",EDGE,"E53")])]})])],"derivedFrom":makeQuery(id+"F7m0HWUFy6dzAhm_1.boolean.opBoolean","MERGE",EDGE,{"derivedFrom":[makeQuery(id+"F1.opExtrude","SWEPT_EDGE",EDGE,{"disambiguationData":[OSD([subQ1,subQ0])]}),makeQuery(id+"F7m0HWUFy6dzAhm_1.opExtrude","SWEPT_EDGE",EDGE,{"disambiguationData":[OSD([subQ1,subQ0])]})]})});}
            var Q17;
            {var subQ0=sQuery(id+"F0.wireOp",EDGE,"E6.5");var subQ1=sQuery(id+"F0.wireOp",EDGE,"E6.4");Q17=makeQuery(id+"F8.boolean.opBoolean","SPLIT",EDGE,{"disambiguationData":[TD([makeQuery(id+"F8.opExtrude","SWEPT_FACE",FACE,{"disambiguationData":[OSD([sQuery(id+"F7.wireOp",EDGE,"E49")])]})])],"derivedFrom":makeQuery(id+"F7m0HWUFy6dzAhm_1.boolean.opBoolean","MERGE",EDGE,{"derivedFrom":[makeQuery(id+"F1.opExtrude","SWEPT_EDGE",EDGE,{"disambiguationData":[OSD([subQ1,subQ0])]}),makeQuery(id+"F7m0HWUFy6dzAhm_1.opExtrude","SWEPT_EDGE",EDGE,{"disambiguationData":[OSD([subQ1,subQ0])]})]})});}
            var Q18;
            {var subQ0=sQuery(id+"F0.wireOp",EDGE,"E6.5");var subQ1=sQuery(id+"F0.wireOp",EDGE,"E6.4");Q18=makeQuery(id+"F8.boolean.opBoolean","SPLIT",EDGE,{"disambiguationData":[TD([makeQuery(id+"F8.opExtrude","SWEPT_FACE",FACE,{"disambiguationData":[OSD([sQuery(id+"F7.wireOp",EDGE,"E45")])]})])],"derivedFrom":makeQuery(id+"F7m0HWUFy6dzAhm_1.boolean.opBoolean","MERGE",EDGE,{"derivedFrom":[makeQuery(id+"F1.opExtrude","SWEPT_EDGE",EDGE,{"disambiguationData":[OSD([subQ1,subQ0])]}),makeQuery(id+"F7m0HWUFy6dzAhm_1.opExtrude","SWEPT_EDGE",EDGE,{"disambiguationData":[OSD([subQ1,subQ0])]})]})});}
            var Q19;
            {var subQ0=sQuery(id+"F0.wireOp",EDGE,"E6.5");var subQ1=sQuery(id+"F0.wireOp",EDGE,"E6.4");Q19=makeQuery(id+"F8.boolean.opBoolean","SPLIT",EDGE,{"disambiguationData":[TD([makeQuery(id+"F8.opExtrude","SWEPT_FACE",FACE,{"disambiguationData":[OSD([sQuery(id+"F7.wireOp",EDGE,"E40")])]})])],"derivedFrom":makeQuery(id+"F7m0HWUFy6dzAhm_1.boolean.opBoolean","MERGE",EDGE,{"derivedFrom":[makeQuery(id+"F1.opExtrude","SWEPT_EDGE",EDGE,{"disambiguationData":[OSD([subQ1,subQ0])]}),makeQuery(id+"F7m0HWUFy6dzAhm_1.opExtrude","SWEPT_EDGE",EDGE,{"disambiguationData":[OSD([subQ1,subQ0])]})]})});}
            var Q20;
            {var subQ0=sQuery(id+"F0.wireOp",EDGE,"E6.5");var subQ1=sQuery(id+"F0.wireOp",EDGE,"E6.4");Q20=makeQuery(id+"F8.boolean.opBoolean","SPLIT",EDGE,{"disambiguationData":[TD([makeQuery(id+"F8.opExtrude","SWEPT_FACE",FACE,{"disambiguationData":[OSD([sQuery(id+"F7.wireOp",EDGE,"E36")])]})])],"derivedFrom":makeQuery(id+"F7m0HWUFy6dzAhm_1.boolean.opBoolean","MERGE",EDGE,{"derivedFrom":[makeQuery(id+"F1.opExtrude","SWEPT_EDGE",EDGE,{"disambiguationData":[OSD([subQ1,subQ0])]}),makeQuery(id+"F7m0HWUFy6dzAhm_1.opExtrude","SWEPT_EDGE",EDGE,{"disambiguationData":[OSD([subQ1,subQ0])]})]})});}
            var Q21;
            {var subQ0=sQuery(id+"F0.wireOp",EDGE,"E6.5");var subQ1=sQuery(id+"F0.wireOp",EDGE,"E6.4");Q21=makeQuery(id+"F8.boolean.opBoolean","SPLIT",EDGE,{"disambiguationData":[TD([makeQuery(id+"F8.opExtrude","SWEPT_FACE",FACE,{"disambiguationData":[OSD([sQuery(id+"F7.wireOp",EDGE,"E35")])]})])],"derivedFrom":makeQuery(id+"F7m0HWUFy6dzAhm_1.boolean.opBoolean","MERGE",EDGE,{"derivedFrom":[makeQuery(id+"F1.opExtrude","SWEPT_EDGE",EDGE,{"disambiguationData":[OSD([subQ1,subQ0])]}),makeQuery(id+"F7m0HWUFy6dzAhm_1.opExtrude","SWEPT_EDGE",EDGE,{"disambiguationData":[OSD([subQ1,subQ0])]})]})});}
            var Q22;
            {var subQ0=sQuery(id+"F0.wireOp",EDGE,"E6.4");var subQ1=sQuery(id+"F0.wireOp",EDGE,"E6.3");Q22=makeQuery(id+"F3.boolean.opBoolean","SPLIT",EDGE,{"disambiguationData":[TD([makeQuery(id+"F3.opExtrude","SWEPT_FACE",FACE,{"disambiguationData":[OSD([sQuery(id+"F2.wireOp",EDGE,"E10")])]})])],"derivedFrom":makeQuery(id+"F1.opExtrude","SWEPT_EDGE",EDGE,{"disambiguationData":[OSD([subQ1,subQ0])]})});}
            var Q23;
            {var subQ0=sQuery(id+"F0.wireOp",EDGE,"E6.3");var subQ2=makeQuery(id+"F3.opExtrude","SWEPT_FACE",FACE,{"disambiguationData":[OSD([sQuery(id+"F2.wireOp",EDGE,"E11")])]});var subQ3=sQuery(id+"F0.wireOp",EDGE,"E6.4");Q23=makeQuery(id+"F5.boolean.opBoolean","SPLIT",EDGE,{"disambiguationData":[TD([makeQuery(id+"F3.boolean.opBoolean","COPY",FACE,{"derivedFrom":subQ2})])],"derivedFrom":makeQuery(id+"F3.boolean.opBoolean","SPLIT",EDGE,{"disambiguationData":[TD([subQ2])],"derivedFrom":makeQuery(id+"F1.opExtrude","SWEPT_EDGE",EDGE,{"disambiguationData":[OSD([subQ0,subQ3])]})})});}
            var Q24;
            {var subQ0=sQuery(id+"F0.wireOp",EDGE,"E6.3");var subQ2=sQuery(id+"F0.wireOp",EDGE,"E6.4");Q24=makeQuery(id+"F5.boolean.opBoolean","SPLIT",EDGE,{"disambiguationData":[TD([makeQuery(id+"F5.opExtrude","SWEPT_FACE",FACE,{"disambiguationData":[OSD([sQuery(id+"F4.wireOp",EDGE,"E16")])]})])],"derivedFrom":makeQuery(id+"F3.boolean.opBoolean","SPLIT",EDGE,{"disambiguationData":[TD([makeQuery(id+"F3.opExtrude","SWEPT_FACE",FACE,{"disambiguationData":[OSD([sQuery(id+"F2.wireOp",EDGE,"E11")])]})])],"derivedFrom":makeQuery(id+"F1.opExtrude","SWEPT_EDGE",EDGE,{"disambiguationData":[OSD([subQ0,subQ2])]})})});}
            var Q25;
            {var subQ0=sQuery(id+"F0.wireOp",EDGE,"E6.3");var subQ2=sQuery(id+"F0.wireOp",EDGE,"E6.4");Q25=makeQuery(id+"F5.boolean.opBoolean","SPLIT",EDGE,{"disambiguationData":[TD([makeQuery(id+"F5.opExtrude","SWEPT_FACE",FACE,{"disambiguationData":[OSD([sQuery(id+"F4.wireOp",EDGE,"E20")])]})])],"derivedFrom":makeQuery(id+"F3.boolean.opBoolean","SPLIT",EDGE,{"disambiguationData":[TD([makeQuery(id+"F3.opExtrude","SWEPT_FACE",FACE,{"disambiguationData":[OSD([sQuery(id+"F2.wireOp",EDGE,"E11")])]})])],"derivedFrom":makeQuery(id+"F1.opExtrude","SWEPT_EDGE",EDGE,{"disambiguationData":[OSD([subQ0,subQ2])]})})});}
            var Q26;
            {var subQ0=sQuery(id+"F0.wireOp",EDGE,"E6.3");var subQ2=sQuery(id+"F0.wireOp",EDGE,"E6.4");Q26=makeQuery(id+"F5.boolean.opBoolean","SPLIT",EDGE,{"disambiguationData":[TD([makeQuery(id+"F5.opExtrude","SWEPT_FACE",FACE,{"disambiguationData":[OSD([sQuery(id+"F4.wireOp",EDGE,"E24")])]})])],"derivedFrom":makeQuery(id+"F3.boolean.opBoolean","SPLIT",EDGE,{"disambiguationData":[TD([makeQuery(id+"F3.opExtrude","SWEPT_FACE",FACE,{"disambiguationData":[OSD([sQuery(id+"F2.wireOp",EDGE,"E11")])]})])],"derivedFrom":makeQuery(id+"F1.opExtrude","SWEPT_EDGE",EDGE,{"disambiguationData":[OSD([subQ0,subQ2])]})})});}
            var Q27;
            {var subQ0=sQuery(id+"F0.wireOp",EDGE,"E6.3");var subQ2=sQuery(id+"F0.wireOp",EDGE,"E6.4");Q27=makeQuery(id+"F5.boolean.opBoolean","SPLIT",EDGE,{"disambiguationData":[TD([makeQuery(id+"F5.opExtrude","SWEPT_FACE",FACE,{"disambiguationData":[OSD([sQuery(id+"F4.wireOp",EDGE,"E28")])]})])],"derivedFrom":makeQuery(id+"F3.boolean.opBoolean","SPLIT",EDGE,{"disambiguationData":[TD([makeQuery(id+"F3.opExtrude","SWEPT_FACE",FACE,{"disambiguationData":[OSD([sQuery(id+"F2.wireOp",EDGE,"E11")])]})])],"derivedFrom":makeQuery(id+"F1.opExtrude","SWEPT_EDGE",EDGE,{"disambiguationData":[OSD([subQ0,subQ2])]})})});}
            var Q28;
            {var subQ0=sQuery(id+"F0.wireOp",EDGE,"E6.4");var subQ1=sQuery(id+"F0.wireOp",EDGE,"E6.3");Q28=makeQuery(id+"F7m0HWUFy6dzAhm_1.boolean.opBoolean","MERGE",EDGE,{"derivedFrom":[makeQuery(id+"F5.boolean.opBoolean","SPLIT",EDGE,{"disambiguationData":[TD([makeQuery(id+"F5.opExtrude","SWEPT_FACE",FACE,{"disambiguationData":[OSD([sQuery(id+"F4.wireOp",EDGE,"E32")])]})])],"derivedFrom":makeQuery(id+"F3.boolean.opBoolean","SPLIT",EDGE,{"disambiguationData":[TD([makeQuery(id+"F3.opExtrude","SWEPT_FACE",FACE,{"disambiguationData":[OSD([sQuery(id+"F2.wireOp",EDGE,"E11")])]})])],"derivedFrom":makeQuery(id+"F1.opExtrude","SWEPT_EDGE",EDGE,{"disambiguationData":[OSD([subQ1,subQ0])]})})}),makeQuery(id+"F7m0HWUFy6dzAhm_1.opExtrude","SWEPT_EDGE",EDGE,{"disambiguationData":[OSD([subQ1,subQ0])]})]});}
            fillet(context, id + "F10", {"entities" : qUnion([Q0, Q1, Q2, Q3, Q4, Q5, Q6, Q7, Q8, Q9, Q10, Q11, Q12, Q13, Q14, Q15, Q16, Q17, Q18, Q19, Q20, Q21, Q22, Q23, Q24, Q25, Q26, Q27, Q28]), "radius" : 1.27 * mm, "tangentPropagation" : true, "allowEdgeOverflow" : false});
        }
        {
            var Q0;
            Q0=makeQuery(id+"F1.opExtrude","SWEPT_FACE",FACE,{"disambiguationData":[OSD([sQuery(id+"F0.wireOp",EDGE,"E5")])]});
            var sketch = newSketch(context, id + "F11", { "sketchPlane" : qUnion([Q0])});
            skArc(sketch, "E59", {"start": v(-180.18, 27.3) * mm, "mid": v(-182.56, 29.69) * mm, "end": v(-184.94, 27.3) * mm});
            skArc(sketch, "E60", {"start": v(-34.13, 27.3) * mm, "mid": v(-36.51, 29.69) * mm, "end": v(-38.9, 27.3) * mm});
            skArc(sketch, "E61", {"start": v(-184.94, 15.55) * mm, "mid": v(-182.56, 6.67) * mm, "end": v(-180.18, 15.55) * mm});
            skArc(sketch, "E62", {"start": v(-38.9, 15.55) * mm, "mid": v(-36.51, 6.67) * mm, "end": v(-34.13, 15.55) * mm});
            skLineSegment(sketch, "E63", {"start": v(-180.18, 27.3) * mm, "end": v(-180.18, 15.55) * mm});
            skLineSegment(sketch, "E64", {"start": v(-184.94, 27.3) * mm, "end": v(-184.94, 15.55) * mm});
            skLineSegment(sketch, "E65", {"start": v(-38.9, 27.3) * mm, "end": v(-38.9, 15.55) * mm});
            skLineSegment(sketch, "E66", {"start": v(-34.13, 27.3) * mm, "end": v(-34.13, 15.55) * mm});
            skSolve(sketch);
        }
        {
            var Q0;
            Q0 = qSketchRegion(id + "F11", true);
            extrude(context, id + "F12", {"entities" : qUnion([Q0]), "operationType" : NewBodyOperationType.REMOVE, "oppositeDirection" : true, "depth" : 8.13 * mm});
        }
    });
